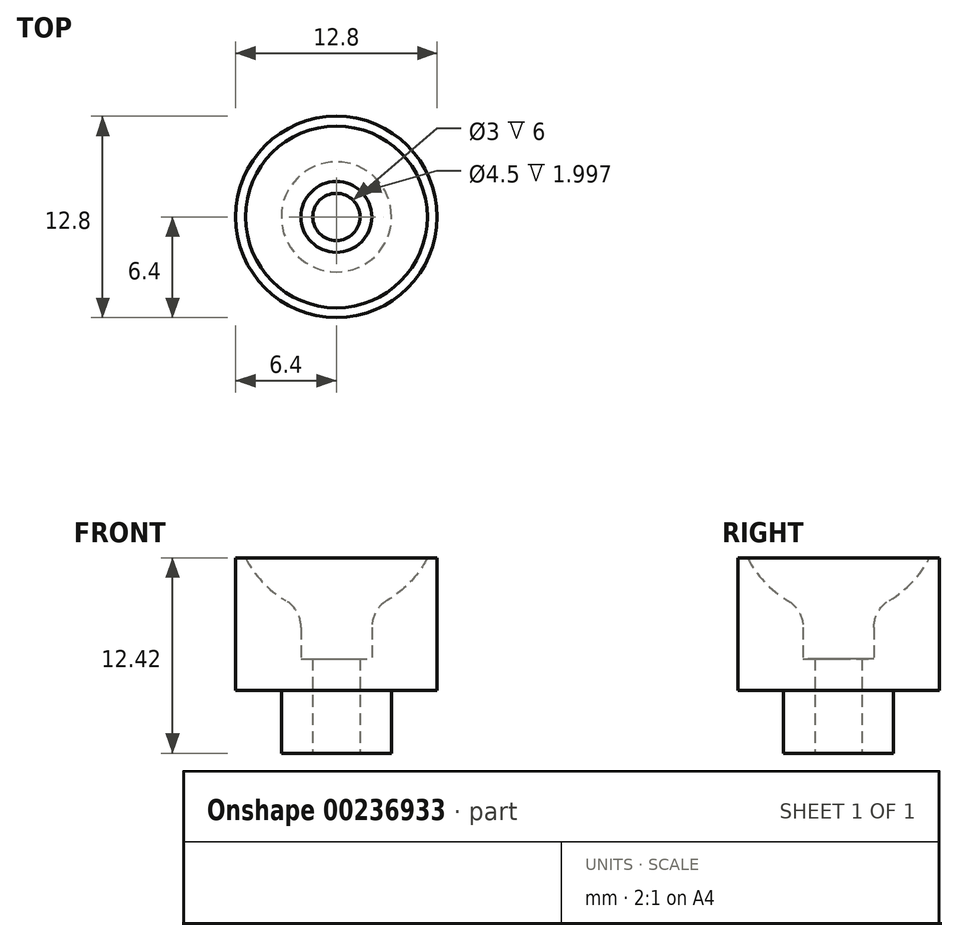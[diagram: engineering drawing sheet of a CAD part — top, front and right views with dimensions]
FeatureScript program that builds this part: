
annotation { "Feature Type Name" : "Feature", "Feature Type Description" : "" }
export const myFeature = defineFeature(function(context is Context, id is Id, definition is map)
    precondition{}
    {
        {
            var Q0;
            Q0=qCreatedBy(makeId("Top.planeOp"),FACE);
            var sketch = newSketch(context, id + "F0", { "sketchPlane" : qUnion([Q0])});
            skCircle(sketch, "E0", {"center": v(0, 0) * mm, "radius": 6.4 * mm});
            skSolve(sketch);
        }
        {
            var Q0;
            Q0 = qSketchRegion(id + "F0", true);
            extrude(context, id + "F1", {"entities" : qUnion([Q0]), "depth" : 11.3 * mm});
        }
        {
            var Q0;
            Q0=qCreatedBy(makeId("Front.planeOp"),FACE);
            var sketch = newSketch(context, id + "F2", { "sketchPlane" : qUnion([Q0])});
            skCircle(sketch, "E1", {"center": v(0, 11.3) * mm, "radius": 6.45 * mm});
            skLineSegment(sketch, "E2", {"start": v(0, 17.75) * mm, "end": v(0, 4.85) * mm});
            skSolve(sketch);
        }
        {
            var Q0;
            {var subQ0=sQuery(id+"F2.wireOp",EDGE,"E2");Q0=makeQuery(id+"F2.imprint","IMPRINT",FACE,{"disambiguationData":[TD([[makeQuery(id+"F2.imprint","IMPRINT",EDGE,{"derivedFrom":subQ0}),1.0]])]});}
            var Q1;
            Q1=sQuery(id+"F2.wireOp",EDGE,"E2");
            revolve(context, id + "F3", {"operationType" : NewBodyOperationType.REMOVE, "entities" : qUnion([Q0]), "axis" : qUnion([Q1]), "revolveType" : RevolveType.FULL, "oppositeDirection" : true});
        }
        {
            var Q0;
            Q0=makeQuery(id+"F3.boolean.opBoolean","INTERSECT",EDGE,{"derivedFrom":[makeQuery(id+"F1.opExtrude","SWEPT_FACE",FACE,{"disambiguationData":[OSD([sQuery(id+"F0.wireOp",EDGE,"E0")])]}),makeQuery(id+"F3.opRevolve","SWEPT_FACE",FACE,{"disambiguationData":[OSD([sQuery(id+"F2.wireOp",EDGE,"E1")])]})]});
            chamfer(context, id + "F4", {"entities" : qUnion([Q0]), "chamferType" : ChamferType.OFFSET_ANGLE, "width" : 5 * mm, "oppositeDirection" : false, "angle" : 90 * degree, "tangentPropagation" : true});
        }
        {
            var Q0;
            Q0=makeQuery(id+"F1.opExtrude","CAP_FACE",FACE,{"disambiguationData":[OSD([sQuery(id+"F0.wireOp",EDGE,"E0")])],"isStart":true});
            var sketch = newSketch(context, id + "F5", { "sketchPlane" : qUnion([Q0])});
            skCircle(sketch, "E3", {"center": v(0, 0) * mm, "radius": 3.5 * mm});
            skSolve(sketch);
        }
        {
            var Q0;
            Q0 = qSketchRegion(id + "F5", true);
            extrude(context, id + "F6", {"entities" : qUnion([Q0]), "operationType" : NewBodyOperationType.ADD, "depth" : 4 * mm});
        }
        {
            var Q0;
            Q0=makeQuery(id+"F6.opExtrude","CAP_FACE",FACE,{"disambiguationData":[OSD([sQuery(id+"F5.wireOp",EDGE,"E3")])],"isStart":false});
            var sketch = newSketch(context, id + "F7", { "sketchPlane" : qUnion([Q0])});
            skCircle(sketch, "E4", {"center": v(0, 0) * mm, "radius": 1.5 * mm});
            skSolve(sketch);
        }
        {
            var Q0;
            Q0 = qSketchRegion(id + "F7", true);
            extrude(context, id + "F8", {"entities" : qUnion([Q0]), "operationType" : NewBodyOperationType.REMOVE, "oppositeDirection" : true, "depth" : 25 * mm});
        }
        {
            var Q0;
            Q0=makeQuery(id+"F6.opExtrude","CAP_FACE",FACE,{"disambiguationData":[OSD([sQuery(id+"F5.wireOp",EDGE,"E3")])],"isStart":false});
            var sketch = newSketch(context, id + "F9", { "sketchPlane" : qUnion([Q0])});
            skCircle(sketch, "E5", {"center": v(0, 0) * mm, "radius": 2.25 * mm});
            skSolve(sketch);
        }
        {
            var Q0;
            Q0 = qSketchRegion(id + "F9", true);
            extrude(context, id + "F10", {"entities" : qUnion([Q0]), "operationType" : NewBodyOperationType.REMOVE, "oppositeDirection" : true, "depth" : 25 * mm, "hasSecondDirection" : true, "secondDirectionOppositeDirection" : true, "secondDirectionDepth" : 6 * mm});
        }
        {
            var Q0;
            Q0=makeQuery(id+"F10.boolean.opBoolean","INTERSECT",EDGE,{"derivedFrom":[makeQuery(id+"F3.boolean.opBoolean","COPY",FACE,{"derivedFrom":makeQuery(id+"F3.opRevolve","SWEPT_FACE",FACE,{"disambiguationData":[OSD([sQuery(id+"F2.wireOp",EDGE,"E1")])]})}),makeQuery(id+"F10.opExtrude","SWEPT_FACE",FACE,{"disambiguationData":[OSD([sQuery(id+"F9.wireOp",EDGE,"E5")])]})]});
            fillet(context, id + "F11", {"entities" : qUnion([Q0]), "radius" : 2 * mm, "tangentPropagation" : true, "allowEdgeOverflow" : false});
        }
    });
